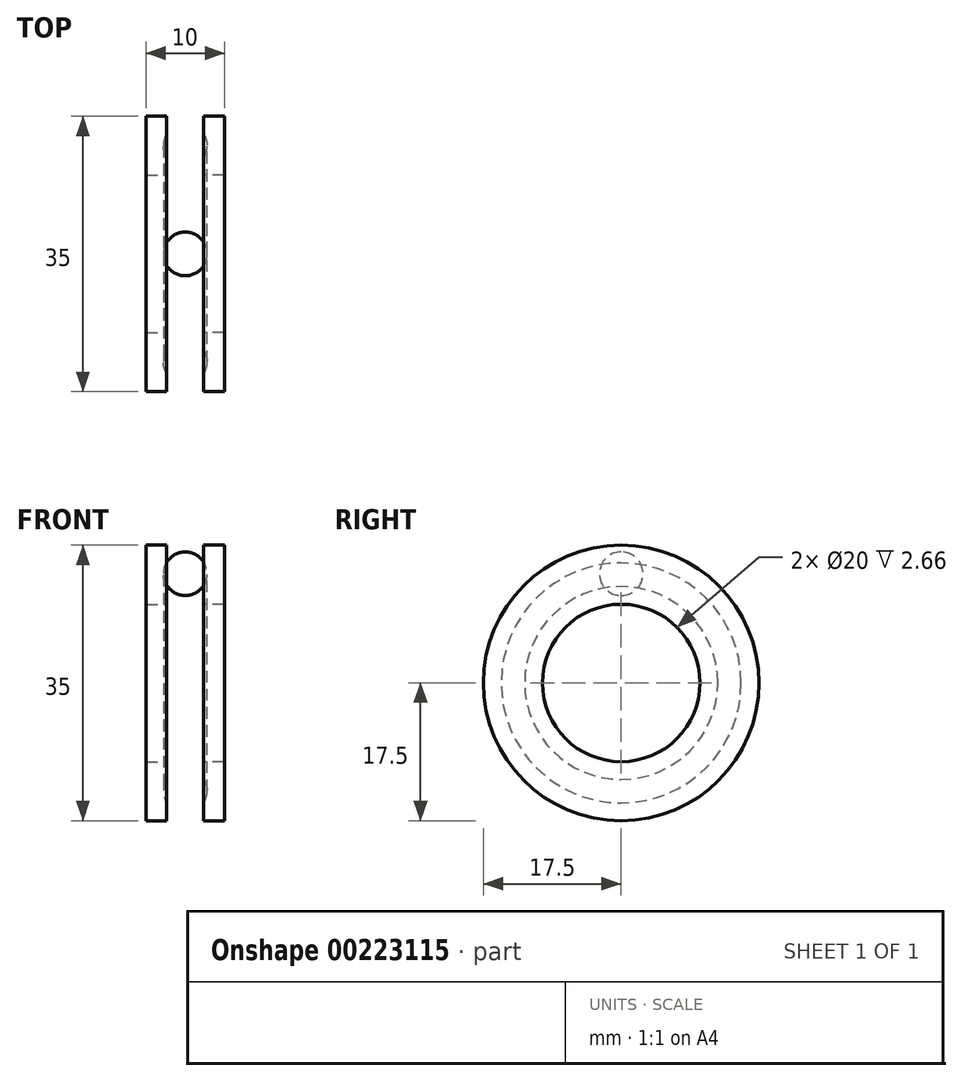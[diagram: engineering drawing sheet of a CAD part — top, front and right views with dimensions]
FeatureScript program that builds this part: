
annotation { "Feature Type Name" : "Feature", "Feature Type Description" : "" }
export const myFeature = defineFeature(function(context is Context, id is Id, definition is map)
    precondition{}
    {
        {
            var Q0;
            Q0=qCreatedBy(makeId("Front.planeOp"),FACE);
            var sketch = newSketch(context, id + "F0", { "sketchPlane" : qUnion([Q0])});
            skLineSegment(sketch, "E0.bottom", {"start": v(0, 10) * mm, "end": v(-2.66, 10) * mm});
            skLineSegment(sketch, "E0.top", {"start": v(0, 17.5) * mm, "end": v(-2.66, 17.5) * mm});
            skLineSegment(sketch, "E0.left", {"start": v(0, 10) * mm, "end": v(0, 17.5) * mm});
            skLineSegment(sketch, "E1", {"start": v(0, 13.75) * mm, "end": v(-5, 13.75) * mm, "construction": true});
            skArc(sketch, "E2", {"start": v(-2.66, 15.24) * mm, "mid": v(-2.22, 13.75) * mm, "end": v(-2.66, 12.26) * mm});
            skLineSegment(sketch, "E3", {"start": v(-2.66, 17.5) * mm, "end": v(-2.66, 15.24) * mm});
            skLineSegment(sketch, "E4", {"start": v(-2.66, 12.26) * mm, "end": v(-2.66, 10) * mm});
            skLineSegment(sketch, "E5.bottom", {"start": v(-2.66, 10) * mm, "end": v(0, 10) * mm});
            skLineSegment(sketch, "E5.top", {"start": v(-2.66, 0) * mm, "end": v(0, 0) * mm, "construction": true});
            skLineSegment(sketch, "E5.left", {"start": v(-2.66, 10) * mm, "end": v(-2.66, 0) * mm, "construction": true});
            skLineSegment(sketch, "E5.right", {"start": v(0, 10) * mm, "end": v(0, 0) * mm, "construction": true});
            skSolve(sketch);
        }
        {
            var Q0;
            Q0 = qSketchRegion(id + "F0", true);
            var Q1;
            Q1=sQuery(id+"F0.wireOp",EDGE,"E5.top");
            revolve(context, id + "F1", {"entities" : qUnion([Q0]), "axis" : qUnion([Q1]), "revolveType" : RevolveType.FULL});
        }
        {
            var Q0;
            Q0=qCreatedBy(makeId("Front.planeOp"),FACE);
            var sketch = newSketch(context, id + "F2", { "sketchPlane" : qUnion([Q0])});
            skLineSegment(sketch, "E6.bottom", {"start": v(-7.34, 10) * mm, "end": v(-10, 10) * mm});
            skLineSegment(sketch, "E6.top", {"start": v(-7.34, 17.5) * mm, "end": v(-10, 17.5) * mm});
            skLineSegment(sketch, "E6.left", {"start": v(-10, 10) * mm, "end": v(-10, 17.5) * mm});
            skLineSegment(sketch, "E7", {"start": v(-5, 13.75) * mm, "end": v(-10, 13.75) * mm, "construction": true});
            skLineSegment(sketch, "E8", {"start": v(-7.34, 17.5) * mm, "end": v(-7.34, 15.24) * mm});
            skLineSegment(sketch, "E9", {"start": v(-7.34, 12.26) * mm, "end": v(-7.34, 10) * mm});
            skLineSegment(sketch, "E10.bottom", {"start": v(-10, 10) * mm, "end": v(-7.34, 10) * mm});
            skLineSegment(sketch, "E10.top", {"start": v(-10, 0) * mm, "end": v(-7.34, 0) * mm, "construction": true});
            skLineSegment(sketch, "E10.left", {"start": v(-7.34, 10) * mm, "end": v(-7.34, 0) * mm, "construction": true});
            skLineSegment(sketch, "E10.right", {"start": v(-10, 10) * mm, "end": v(-10, 0) * mm, "construction": true});
            skLineSegment(sketch, "E11.bottom", {"start": v(0, 0) * mm, "end": v(-10, 0) * mm, "construction": true});
            skLineSegment(sketch, "E11.top", {"start": v(0, 17.5) * mm, "end": v(-10, 17.5) * mm, "construction": true});
            skLineSegment(sketch, "E11.left", {"start": v(0, 0) * mm, "end": v(0, 17.5) * mm, "construction": true});
            skLineSegment(sketch, "E11.right", {"start": v(-10, 0) * mm, "end": v(-10, 17.5) * mm, "construction": true});
            skArc(sketch, "E12", {"start": v(-7.34, 15.24) * mm, "mid": v(-7.77, 13.75) * mm, "end": v(-7.34, 12.26) * mm});
            skSolve(sketch);
        }
        {
            var Q0;
            Q0 = qSketchRegion(id + "F2", true);
            var Q1;
            Q1=sQuery(id+"F2.wireOp",EDGE,"E11.bottom");
            revolve(context, id + "F3", {"entities" : qUnion([Q0]), "axis" : qUnion([Q1]), "revolveType" : RevolveType.FULL});
        }
        {
            var Q0;
            Q0=qCreatedBy(makeId("Right.planeOp"),FACE);
            var sketch = newSketch(context, id + "F4", { "sketchPlane" : qUnion([Q0])});
            skArc(sketch, "E13", {"start": v(0, 11.1) * mm, "mid": v(2.77, 13.87) * mm, "end": v(0, 16.65) * mm});
            skLineSegment(sketch, "E14.bottom", {"start": v(0, 0) * mm, "end": v(2.78, 0) * mm, "construction": true});
            skLineSegment(sketch, "E14.top", {"start": v(0, 13.88) * mm, "end": v(2.77, 13.88) * mm, "construction": true});
            skLineSegment(sketch, "E14.left", {"start": v(0, 0) * mm, "end": v(0, 13.88) * mm, "construction": true});
            skLineSegment(sketch, "E14.right", {"start": v(2.78, 0) * mm, "end": v(2.77, 13.88) * mm, "construction": true});
            skLineSegment(sketch, "E15", {"start": v(0, 16.65) * mm, "end": v(0, 11.1) * mm});
            skSolve(sketch);
        }
        {
            var Q0;
            Q0 = qSketchRegion(id + "F4", true);
            var Q1;
            Q1=sQuery(id+"F4.wireOp",EDGE,"E15");
            revolve(context, id + "F5", {"entities" : qUnion([Q0]), "axis" : qUnion([Q1]), "revolveType" : RevolveType.FULL});
        }
        {
            var Q0;
            Q0=makeQuery(id+"F5.opRevolve","SWEPT_BODY",BODY,{"disambiguationData":[OSD([sQuery(id+"F4.wireOp",EDGE,"E13"),sQuery(id+"F4.wireOp",EDGE,"E15")])]});
            transform(context, id + "F6", {"entities" : qUnion([Q0]), "transformType" : TransformType.TRANSLATION_3D, "dx" : -5 * mm, "dy" : 0 * mm, "dz" : 0 * mm, "makeCopy" : false});
        }
        {
            var Q0;
            Q0=makeQuery(id+"F5.opRevolve","SWEPT_BODY",BODY,{"disambiguationData":[OSD([sQuery(id+"F4.wireOp",EDGE,"E13"),sQuery(id+"F4.wireOp",EDGE,"E15")])]});
            var Q1;
            Q1=makeQuery(id+"F3.opRevolve","SWEPT_EDGE",EDGE,{"disambiguationData":[OSD([sQuery(id+"F2.wireOp",EDGE,"E6.top"),sQuery(id+"F2.wireOp",EDGE,"E8")])]});
            circularPattern(context, id + "F7", {"entities" : qUnion([Q0]), "axis" : qUnion([Q1]), "angle" : 360 * degree, "instanceCount" : 13, "oppositeDirection" : true, "equalSpace" : true});
        }
        {
            var Q0;
            Q0=makeQuery(id+"F7.opPattern","COPY",BODY,{"derivedFrom":makeQuery(id+"F5.opRevolve","SWEPT_BODY",BODY,{"disambiguationData":[OSD([sQuery(id+"F4.wireOp",EDGE,"E13"),sQuery(id+"F4.wireOp",EDGE,"E15")])]}),"instanceName":"1"});
            var Q1;
            Q1=makeQuery(id+"F7.opPattern","COPY",BODY,{"derivedFrom":makeQuery(id+"F5.opRevolve","SWEPT_BODY",BODY,{"disambiguationData":[OSD([sQuery(id+"F4.wireOp",EDGE,"E13"),sQuery(id+"F4.wireOp",EDGE,"E15")])]}),"instanceName":"2"});
            var Q2;
            Q2=makeQuery(id+"F7.opPattern","COPY",BODY,{"derivedFrom":makeQuery(id+"F5.opRevolve","SWEPT_BODY",BODY,{"disambiguationData":[OSD([sQuery(id+"F4.wireOp",EDGE,"E13"),sQuery(id+"F4.wireOp",EDGE,"E15")])]}),"instanceName":"3"});
            var Q3;
            Q3=makeQuery(id+"F7.opPattern","COPY",BODY,{"derivedFrom":makeQuery(id+"F5.opRevolve","SWEPT_BODY",BODY,{"disambiguationData":[OSD([sQuery(id+"F4.wireOp",EDGE,"E13"),sQuery(id+"F4.wireOp",EDGE,"E15")])]}),"instanceName":"4"});
            var Q4;
            Q4=makeQuery(id+"F7.opPattern","COPY",BODY,{"derivedFrom":makeQuery(id+"F5.opRevolve","SWEPT_BODY",BODY,{"disambiguationData":[OSD([sQuery(id+"F4.wireOp",EDGE,"E13"),sQuery(id+"F4.wireOp",EDGE,"E15")])]}),"instanceName":"5"});
            var Q5;
            Q5=makeQuery(id+"F7.opPattern","COPY",BODY,{"derivedFrom":makeQuery(id+"F5.opRevolve","SWEPT_BODY",BODY,{"disambiguationData":[OSD([sQuery(id+"F4.wireOp",EDGE,"E13"),sQuery(id+"F4.wireOp",EDGE,"E15")])]}),"instanceName":"6"});
            var Q6;
            Q6=makeQuery(id+"F7.opPattern","COPY",BODY,{"derivedFrom":makeQuery(id+"F5.opRevolve","SWEPT_BODY",BODY,{"disambiguationData":[OSD([sQuery(id+"F4.wireOp",EDGE,"E13"),sQuery(id+"F4.wireOp",EDGE,"E15")])]}),"instanceName":"7"});
            var Q7;
            Q7=makeQuery(id+"F7.opPattern","COPY",BODY,{"derivedFrom":makeQuery(id+"F5.opRevolve","SWEPT_BODY",BODY,{"disambiguationData":[OSD([sQuery(id+"F4.wireOp",EDGE,"E13"),sQuery(id+"F4.wireOp",EDGE,"E15")])]}),"instanceName":"8"});
            var Q8;
            Q8=makeQuery(id+"F7.opPattern","COPY",BODY,{"derivedFrom":makeQuery(id+"F5.opRevolve","SWEPT_BODY",BODY,{"disambiguationData":[OSD([sQuery(id+"F4.wireOp",EDGE,"E13"),sQuery(id+"F4.wireOp",EDGE,"E15")])]}),"instanceName":"9"});
            var Q9;
            Q9=makeQuery(id+"F7.opPattern","COPY",BODY,{"derivedFrom":makeQuery(id+"F5.opRevolve","SWEPT_BODY",BODY,{"disambiguationData":[OSD([sQuery(id+"F4.wireOp",EDGE,"E13"),sQuery(id+"F4.wireOp",EDGE,"E15")])]}),"instanceName":"10"});
            var Q10;
            Q10=makeQuery(id+"F7.opPattern","COPY",BODY,{"derivedFrom":makeQuery(id+"F5.opRevolve","SWEPT_BODY",BODY,{"disambiguationData":[OSD([sQuery(id+"F4.wireOp",EDGE,"E13"),sQuery(id+"F4.wireOp",EDGE,"E15")])]}),"instanceName":"11"});
            var Q11;
            Q11=makeQuery(id+"F7.opPattern","COPY",BODY,{"derivedFrom":makeQuery(id+"F5.opRevolve","SWEPT_BODY",BODY,{"disambiguationData":[OSD([sQuery(id+"F4.wireOp",EDGE,"E13"),sQuery(id+"F4.wireOp",EDGE,"E15")])]}),"instanceName":"12"});
            deleteBodies(context, id + "F8", {"entities" : qUnion([Q0, Q1, Q2, Q3, Q4, Q5, Q6, Q7, Q8, Q9, Q10, Q11])});
        }
    });
